# Revit family: Furniture_Office-Chairs_Flokk_Giroflex-40
name_source: partatom
category: Furniture
units: mm (PartAtom-declared; Revit-internal decimal feet)

## family parameters
Always vertical = Yes
Cut with Voids When Loaded = No
OmniClass Number = 23.40.20.14.14.11
OmniClass Title = Chairs
Room Calculation Point = No
Shared = No
Work Plane-Based = No

## types (1)
- Giroflex 40
    AssetType = Movable
    BIMObjectName = Furniture_Office-Chairs_Flokk_Giroflex-40
    Brand = Flokk
    Category = Giroflex
    Color = Various
    Cost = 0 $
    Default Elevation = 0 mm  [stored 0 ft]
    Description = The giroflex 40 is a height adjustable mesh-back swivel chair with lumbar support. It has the Giroflex Synchro Motion tilt mechanism and dual-zone seat profile are standard. It can be enhanced with a wide range of options and variants for fast and easy decision making.
    DurationUnit = Year
    HighestSeatingHeight = 500 mm  [stored 1.64042 ft]
    IfcExportAs = IfcFurnishingElementType
    IfcExportType = CHAIR
    LowestSeatingHeight = 500 mm  [stored 1.64042 ft]
    MainColor = Various
    Manufacturer = Flokk
    ManufacturerName = Flokk
    ManufacturerURL = https://www.flokk.com
    Material = Plastic, Metal and Textile
    Model = Giroflex 40
    ModelNumber = 40-4049
    NBSDescription = Stacking chairs
    NBSReference = 45-35-20/355
    Name = Giroflex-40
    NominalDepth = 697 mm
    NominalHeight = 1055 mm
    NominalLength = 713 mm
    OfficeChairQuaternaryMaterial = Black RAL 9005
    ProductInformation = The giroflex 40 is a height adjustable mesh-back swivel chair with lumbar support. It has the Giroflex Synchro Motion tilt mechanism and dual-zone seat profile are standard. It can be enhanced with a wide range of options and variants for fast and easy decision making.
    SeatingHeight = 500 mm  [stored 1.64042 ft]
    Shape = Sculptured
    Size = 715x700x1100 mm
    URL = https://store.flokk.com
    Uniclass2 = Pr_40_50_12_51
    Uniclass2015Description = Meeting room chairs
    Uniclass2015Reference = Pr_40_50_12_51
    Version = 1
    VersionDate = 09/01/2023
    WarrantyDurationUnit = Year

note: [stored X ft] marks values corroborated as IEEE doubles in the binary element streams (Revit-internal decimal feet)

## geometry (parser evidence)
native form markers: Sweep x4
no freeform markers — native parametric forms only
